# Revit family: FP-Revit18-en-RS2474F3LJ1-Freezer-0-US-CA-90002450A
name_source: partatom
category: Specialty Equipment
revit_build: Autodesk Revit 2018 (Build: 20170223_1515(x64)
units: mm (PartAtom-declared; Revit-internal decimal feet)

## family parameters
Always vertical = Yes
Cut with Voids When Loaded = Yes
OmniClass Number = 23.40.40.11.11
OmniClass Title = Refrigerators and Freezers
Part Type = Normal
Room Calculation Point = No
Round Connector Dimension = Use Diameter
Shared = No
Work Plane-Based = No

## types (1)
- RS2474F3LJ1
    Cavity - Depth (600mm min with services external) = 600 mm
    Cavity - Width = 600 mm
    Connector Description - Electrical = 120 V, 60 Hz, 10 A circuit
    Connector Description - Water = min 275 kPa (40 psi) max 827 kPa (120 psi)
    Description = 24" Integrated Freezer
    Manufacturer = Fisher & Paykel Appliances
    Material - Body = Fisher & Paykel - Grey
    Material - Door Structure = Fisher & Paykel - White
    Model = RS2474F3LJ1
    Product - Depth (exl front panel) = 579 mm  [stored 1.89961 ft]
    Product - Width = 592 mm  [stored 1.94226 ft]
    URL = www.fisherpaykel.com

note: [stored X ft] marks values corroborated as IEEE doubles in the binary element streams (Revit-internal decimal feet)

## geometry (parser evidence)
native form markers: Sweep x14
no freeform markers — native parametric forms only
